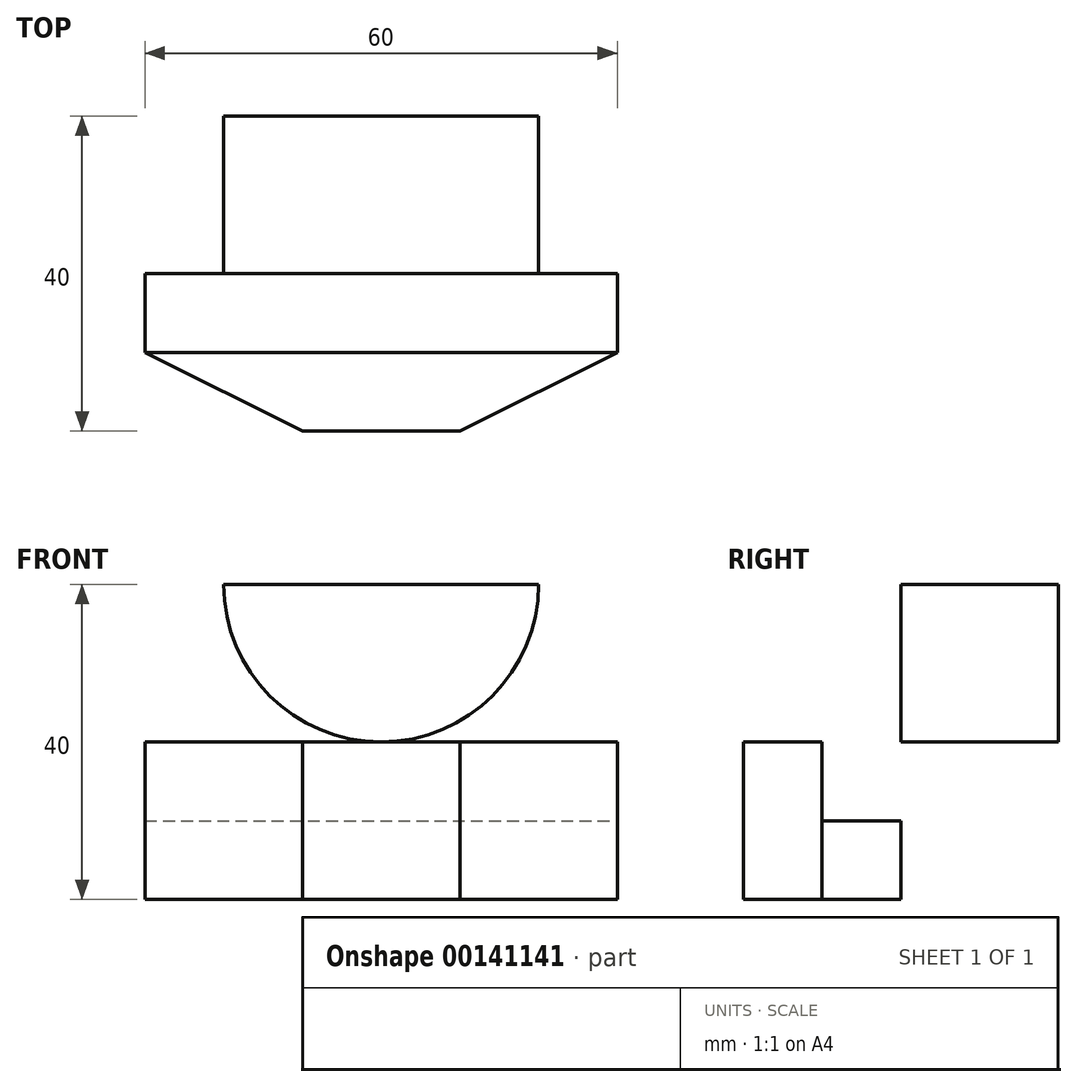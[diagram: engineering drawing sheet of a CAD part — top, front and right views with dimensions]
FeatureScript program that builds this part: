
annotation { "Feature Type Name" : "Feature", "Feature Type Description" : "" }
export const myFeature = defineFeature(function(context is Context, id is Id, definition is map)
    precondition{}
    {
        {
            var Q0;
            Q0=qCreatedBy(makeId("Right.planeOp"),FACE);
            var sketch = newSketch(context, id + "F0", { "sketchPlane" : qUnion([Q0])});
            skLineSegment(sketch, "E0", {"start": v(0, 0) * mm, "end": v(0, 40) * mm});
            skLineSegment(sketch, "E1", {"start": v(0, 40) * mm, "end": v(-20, 40) * mm});
            skLineSegment(sketch, "E2", {"start": v(-20, 40) * mm, "end": v(-20, 10) * mm});
            skLineSegment(sketch, "E3", {"start": v(-20, 10) * mm, "end": v(-30, 10) * mm});
            skLineSegment(sketch, "E4", {"start": v(-30, 10) * mm, "end": v(-30, 20) * mm});
            skLineSegment(sketch, "E5", {"start": v(-30, 20) * mm, "end": v(-40, 20) * mm});
            skLineSegment(sketch, "E6", {"start": v(-40, 20) * mm, "end": v(-40, 0) * mm});
            skLineSegment(sketch, "E7", {"start": v(-40, 0) * mm, "end": v(0, 0) * mm});
            skSolve(sketch);
        }
        {
            var Q0;
            Q0=makeQuery(id+"F0.imprint","IMPRINT",FACE,{"disambiguationData":[TD([[makeQuery(id+"F0.imprint","IMPRINT",EDGE,{"derivedFrom":sQuery(id+"F0.wireOp",EDGE,"E0")}),1.0]])]});
            extrude(context, id + "F1", {"entities" : qUnion([Q0]), "oppositeDirection" : true, "depth" : 60 * mm});
        }
        {
            var Q0;
            Q0=makeQuery(id+"F1.opExtrude","SWEPT_FACE",FACE,{"disambiguationData":[OSD([sQuery(id+"F0.wireOp",EDGE,"E0")])]});
            var sketch = newSketch(context, id + "F2", { "sketchPlane" : qUnion([Q0])});
            skLineSegment(sketch, "E8", {"start": v(30, 50.34) * mm, "end": v(30, 31.23) * mm, "construction": true});
            skArc(sketch, "E9", {"start": v(50, 40) * mm, "mid": v(30, 20) * mm, "end": v(10, 40) * mm});
            skSolve(sketch);
        }
        {
            var Q0;
            {var subQ0=sQuery(id+"F2.wireOp",EDGE,"E9");Q0=makeQuery(id+"F2.imprint","IMPRINT",FACE,{"disambiguationData":[TD([[makeQuery(id+"F2.imprint","IMPRINT",EDGE,{"derivedFrom":subQ0}),-1.0]])]});}
            var Q1;
            Q1=makeQuery(id+"F1.opExtrude","SWEPT_FACE",FACE,{"disambiguationData":[OSD([sQuery(id+"F0.wireOp",EDGE,"E2")])]});
            extrude(context, id + "F3", {"entities" : qUnion([Q0]), "operationType" : NewBodyOperationType.REMOVE, "endBound" : BoundingType.UP_TO_SURFACE, "oppositeDirection" : true, "endBoundEntityFace" : qUnion([Q1]), "depth" : 25 * mm});
        }
        {
            var Q0;
            Q0=makeQuery(id+"F1.opExtrude","SWEPT_FACE",FACE,{"disambiguationData":[OSD([sQuery(id+"F0.wireOp",EDGE,"E5")])]});
            var sketch = newSketch(context, id + "F4", { "sketchPlane" : qUnion([Q0])});
            skLineSegment(sketch, "E10", {"start": v(0, -30) * mm, "end": v(-20, -40) * mm});
            skLineSegment(sketch, "E11", {"start": v(-20, -40) * mm, "end": v(-20, -30) * mm});
            skLineSegment(sketch, "E12", {"start": v(-20, -30) * mm, "end": v(0, -30) * mm});
            skLineSegment(sketch, "E13", {"start": v(-30, 0) * mm, "end": v(-30, 8.62) * mm, "construction": true});
            skLineSegment(sketch, "E14.MirrorCS", {"start": v(-40, -40) * mm, "end": v(-40, -30) * mm});
            skLineSegment(sketch, "E15.MirrorCS", {"start": v(-40, -30) * mm, "end": v(-60, -30) * mm});
            skLineSegment(sketch, "E16.MirrorCS", {"start": v(-60, -30) * mm, "end": v(-40, -40) * mm});
            skSolve(sketch);
        }
        {
            var Q0;
            {var subQ0=sQuery(id+"F4.wireOp",EDGE,"E10");Q0=makeQuery(id+"F4.imprint","IMPRINT",FACE,{"disambiguationData":[TD([[makeQuery(id+"F4.imprint","IMPRINT",EDGE,{"derivedFrom":subQ0}),1.0]])]});}
            var Q1;
            {var subQ0=sQuery(id+"F4.wireOp",EDGE,"E16.MirrorCS");Q1=makeQuery(id+"F4.imprint","IMPRINT",FACE,{"disambiguationData":[TD([[makeQuery(id+"F4.imprint","IMPRINT",EDGE,{"derivedFrom":subQ0}),-1.0]])]});}
            var Q2;
            Q2=makeQuery(id+"F1.opExtrude","SWEPT_FACE",FACE,{"disambiguationData":[OSD([sQuery(id+"F0.wireOp",EDGE,"E7")])]});
            extrude(context, id + "F5", {"entities" : qUnion([Q0, Q1]), "operationType" : NewBodyOperationType.REMOVE, "endBound" : BoundingType.UP_TO_SURFACE, "oppositeDirection" : true, "endBoundEntityFace" : qUnion([Q2]), "depth" : 25 * mm});
        }
    });
